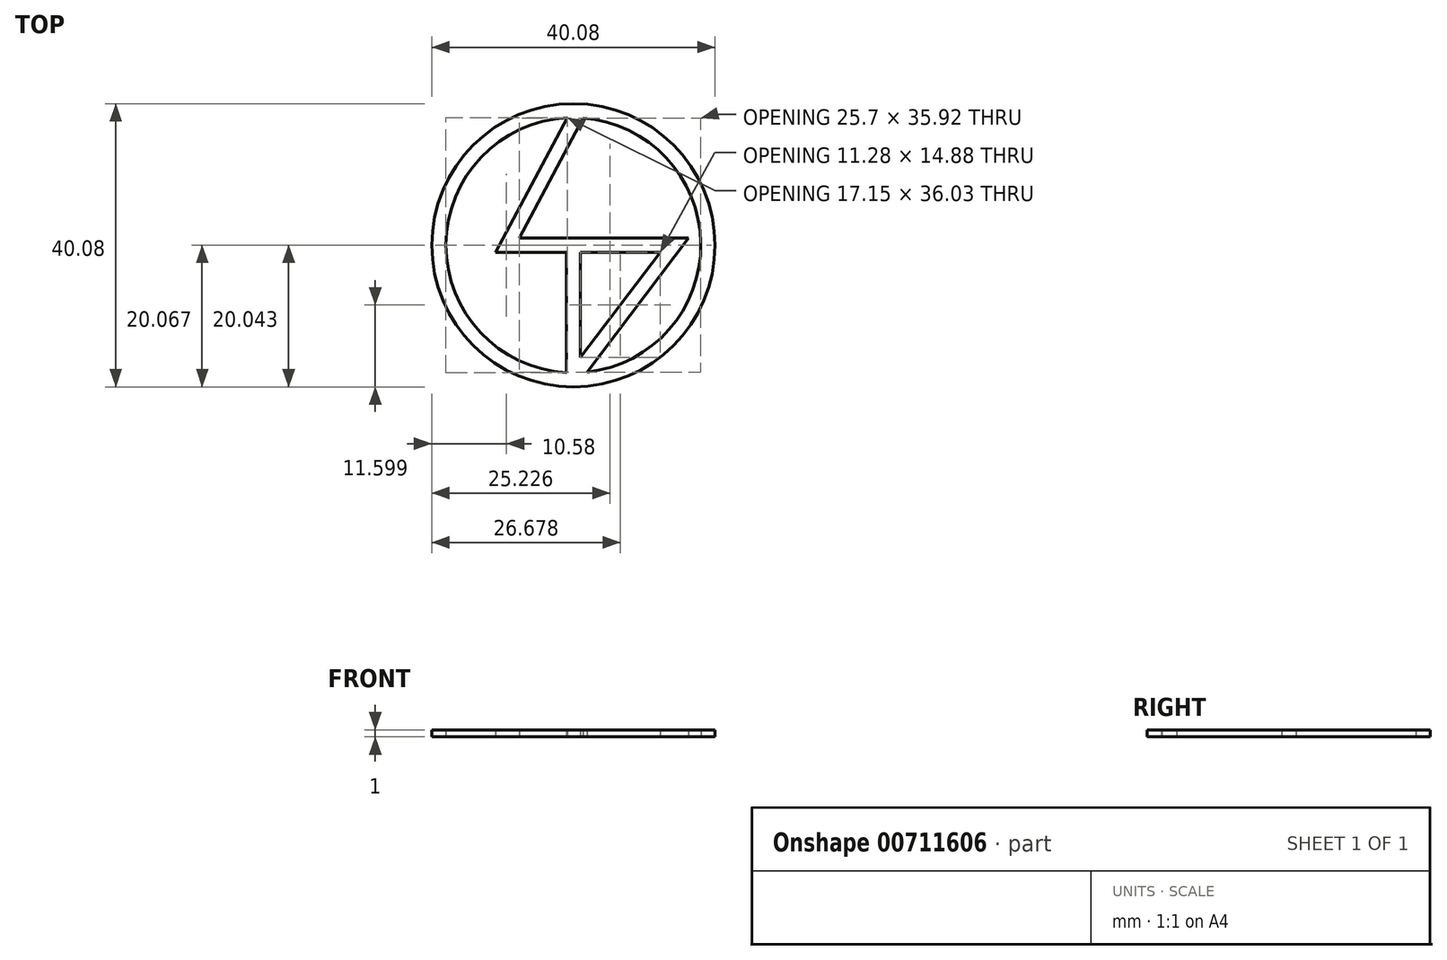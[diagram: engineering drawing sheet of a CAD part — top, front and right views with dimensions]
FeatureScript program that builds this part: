
annotation { "Feature Type Name" : "Feature", "Feature Type Description" : "" }
export const myFeature = defineFeature(function(context is Context, id is Id, definition is map)
    precondition{}
    {
        {
            var Q0;
            Q0=qCreatedBy(makeId("Top.planeOp"),FACE);
            var sketch = newSketch(context, id + "F0", { "sketchPlane" : qUnion([Q0])});
            skLineSegment(sketch, "E0", {"start": v(0, 17.55) * mm, "end": v(-9.33, 0) * mm, "construction": true});
            skLineSegment(sketch, "E1", {"start": v(14.29, 0) * mm, "end": v(0, -18.86) * mm, "construction": true});
            skLineSegment(sketch, "E2", {"start": v(0, -18.86) * mm, "end": v(0, 0) * mm, "construction": true});
            skLineSegment(sketch, "E3", {"start": v(-9.33, 0) * mm, "end": v(0, 0) * mm, "construction": true});
            skLineSegment(sketch, "E4", {"start": v(0, 0) * mm, "end": v(14.29, 0) * mm, "construction": true});
            skLineSegment(sketch, "E5.2", {"start": v(-0.88, 18.02) * mm, "end": v(-11, -1) * mm});
            skLineSegment(sketch, "E6.0", {"start": v(16.3, 1) * mm, "end": v(1.96, -17.93) * mm});
            skLineSegment(sketch, "E6.1", {"start": v(-7.66, 1) * mm, "end": v(16.3, 1) * mm});
            skLineSegment(sketch, "E6.2", {"start": v(0.88, 17.08) * mm, "end": v(-7.66, 1) * mm});
            skLineSegment(sketch, "E7", {"start": v(-11, -1) * mm, "end": v(-1, -1) * mm});
            skLineSegment(sketch, "E8", {"start": v(-0.88, 18.02) * mm, "end": v(0.88, 17.08) * mm});
            skLineSegment(sketch, "E9.0", {"start": v(1, -9.4) * mm, "end": v(1, 0) * mm, "construction": true});
            skLineSegment(sketch, "E10", {"start": v(1, -1) * mm, "end": v(1, -15.88) * mm});
            skLineSegment(sketch, "E11", {"start": v(1, -1) * mm, "end": v(12.28, -1) * mm});
            skLineSegment(sketch, "E12", {"start": v(12.28, -1) * mm, "end": v(1, -15.88) * mm});
            skCircle(sketch, "E13", {"center": v(0, 0) * mm, "radius": 18.04 * mm});
            skLineSegment(sketch, "E14", {"start": v(-1, -18.01) * mm, "end": v(-1, -1) * mm});
            skLineSegment(sketch, "E15", {"start": v(-1, -1) * mm, "end": v(1, -1) * mm, "construction": true});
            skCircle(sketch, "E16", {"center": v(0, 0) * mm, "radius": 20.04 * mm});
            skLineSegment(sketch, "E17", {"start": v(0.88, 17.08) * mm, "end": v(1.37, 17.99) * mm});
            skLineSegment(sketch, "E18", {"start": v(-1, -18.01) * mm, "end": v(-1, -21.83) * mm, "construction": true});
            skLineSegment(sketch, "E19", {"start": v(-1, -21.83) * mm, "end": v(1.96, -17.93) * mm, "construction": true});
            skSolve(sketch);
        }
        {
            var Q0;
            Q0=makeQuery(id+"F0.imprint","IMPRINT",FACE,{"disambiguationData":[TD([[makeQuery(id+"F0.imprint","IMPRINT",EDGE,{"derivedFrom":sQuery(id+"F0.wireOp",EDGE,"E5.2")}),1.0]])]});
            var Q1;
            Q1=makeQuery(id+"F0.imprint","IMPRINT",FACE,{"disambiguationData":[TD([[makeQuery(id+"F0.imprint","IMPRINT",EDGE,{"derivedFrom":sQuery(id+"F0.wireOp",EDGE,"E16")}),1.0]])]});
            var Q2;
            {var subQ0=sQuery(id+"F0.wireOp",EDGE,"E8");Q2=makeQuery(id+"F0.imprint","IMPRINT",FACE,{"disambiguationData":[TD([[makeQuery(id+"F0.imprint","IMPRINT",EDGE,{"derivedFrom":subQ0}),1.0]])]});}
            extrude(context, id + "F1", {"entities" : qUnion([Q0, Q1, Q2]), "depth" : 1 * mm, "offsetDistance" : 25 * mm});
        }
    });
